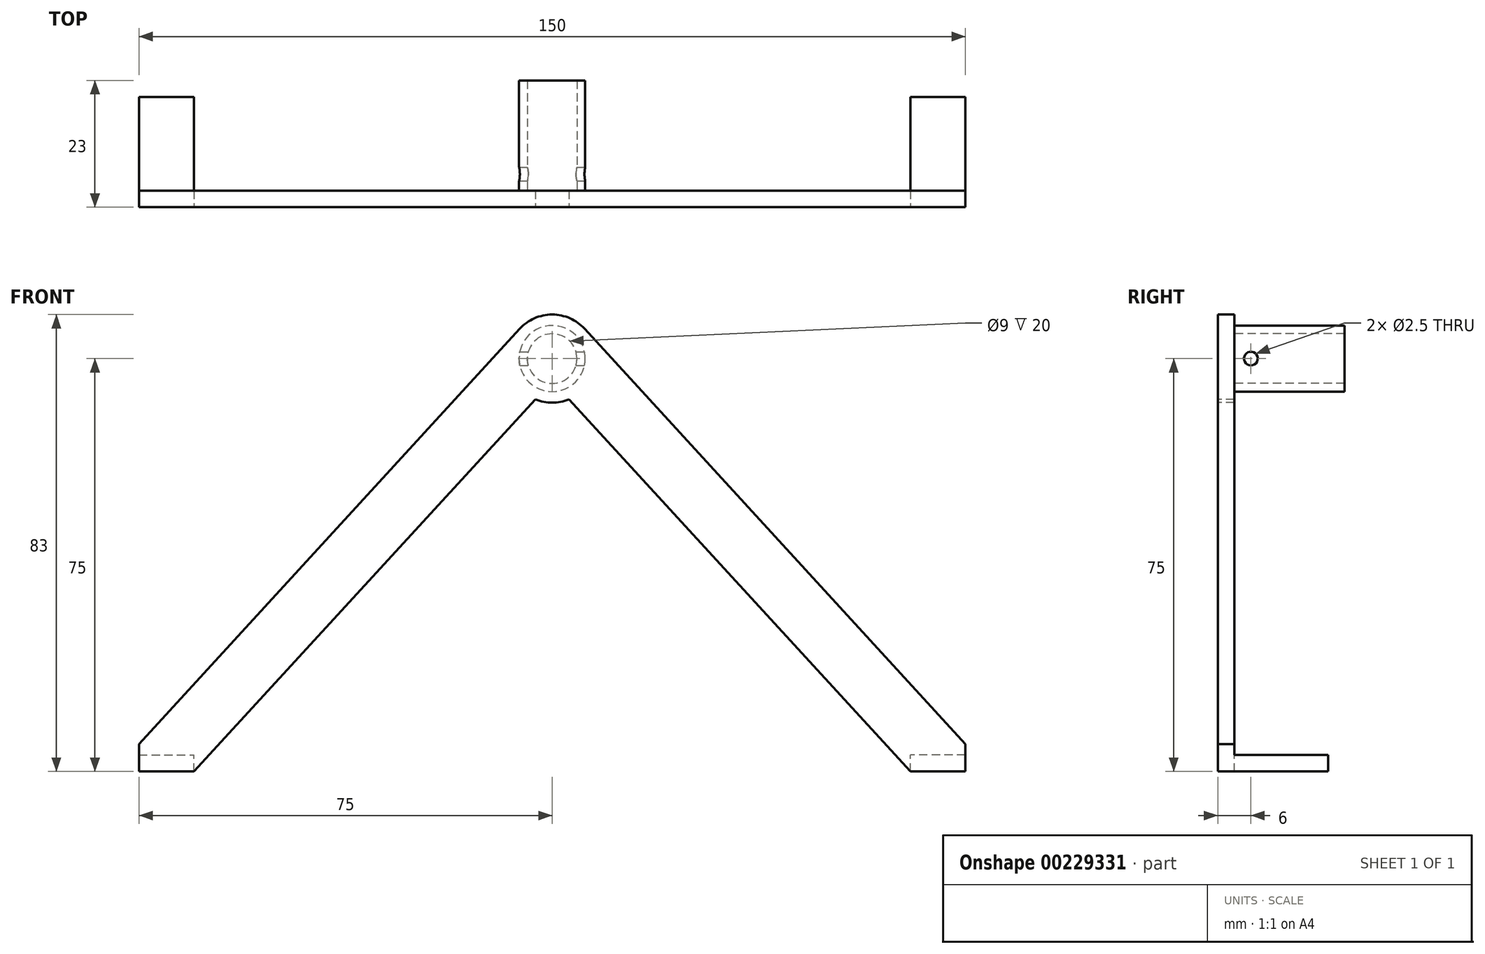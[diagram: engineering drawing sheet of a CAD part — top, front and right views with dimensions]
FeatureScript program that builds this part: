
annotation { "Feature Type Name" : "Feature", "Feature Type Description" : "" }
export const myFeature = defineFeature(function(context is Context, id is Id, definition is map)
    precondition{}
    {
        {
            var Q0;
            Q0=qCreatedBy(makeId("Front.planeOp"),FACE);
            var sketch = newSketch(context, id + "F0", { "sketchPlane" : qUnion([Q0])});
            skLineSegment(sketch, "E0", {"start": v(-75, 0) * mm, "end": v(-65, 0) * mm});
            skLineSegment(sketch, "E1", {"start": v(-75, 0) * mm, "end": v(-75, 5) * mm});
            skLineSegment(sketch, "E2", {"start": v(-75, 5) * mm, "end": v(-5.9, 80.4) * mm});
            skLineSegment(sketch, "E3.MirrorCS", {"start": v(75, 5) * mm, "end": v(5.9, 80.4) * mm});
            skLineSegment(sketch, "E4.MirrorCS", {"start": v(75, 0) * mm, "end": v(75, 5) * mm});
            skCircle(sketch, "E5", {"center": v(0, 75) * mm, "radius": 6 * mm, "construction": true});
            skArc(sketch, "E6", {"start": v(-3.05, 67.6) * mm, "mid": v(0, 67) * mm, "end": v(3.05, 67.6) * mm});
            skLineSegment(sketch, "E7", {"start": v(-65, 0) * mm, "end": v(-3.05, 67.6) * mm});
            skLineSegment(sketch, "E8.MirrorCS", {"start": v(65, 0) * mm, "end": v(3.05, 67.6) * mm});
            skArc(sketch, "E9.trimOffspring", {"start": v(5.9, 80.4) * mm, "mid": v(0, 83) * mm, "end": v(-5.9, 80.4) * mm});
            skLineSegment(sketch, "E10.trimOffspring", {"start": v(65, 0) * mm, "end": v(75, 0) * mm});
            skSolve(sketch);
        }
        {
            var Q0;
            Q0=makeQuery(id+"F0.imprint","IMPRINT",FACE,{"disambiguationData":[TD([[makeQuery(id+"F0.imprint","IMPRINT",EDGE,{"derivedFrom":sQuery(id+"F0.wireOp",EDGE,"E0")}),1.0]])]});
            extrude(context, id + "F1", {"entities" : qUnion([Q0]), "oppositeDirection" : true, "depth" : 3 * mm});
        }
        {
            var Q0;
            Q0=makeQuery(id+"F1.opExtrude","CAP_FACE",FACE,{"disambiguationData":[OSD([sQuery(id+"F0.wireOp",EDGE,"E0"),sQuery(id+"F0.wireOp",EDGE,"E1"),sQuery(id+"F0.wireOp",EDGE,"E2"),sQuery(id+"F0.wireOp",EDGE,"E3.MirrorCS"),sQuery(id+"F0.wireOp",EDGE,"E4.MirrorCS"),sQuery(id+"F0.wireOp",EDGE,"E6"),sQuery(id+"F0.wireOp",EDGE,"E7"),sQuery(id+"F0.wireOp",EDGE,"E8.MirrorCS"),sQuery(id+"F0.wireOp",EDGE,"E9.trimOffspring"),sQuery(id+"F0.wireOp",EDGE,"E10.trimOffspring")])],"isStart":false});
            var sketch = newSketch(context, id + "F2", { "sketchPlane" : qUnion([Q0])});
            skCircle(sketch, "E11", {"center": v(0, 75) * mm, "radius": 6 * mm});
            skCircle(sketch, "E12", {"center": v(0, 75) * mm, "radius": 4.5 * mm});
            skSolve(sketch);
        }
        {
            var Q0;
            Q0 = qSketchRegion(id + "F2", true);
            extrude(context, id + "F3", {"entities" : qUnion([Q0]), "operationType" : NewBodyOperationType.ADD, "depth" : 20 * mm});
        }
        {
            var Q0;
            {var subQ0=sQuery(id+"F0.wireOp",EDGE,"E10.trimOffspring");var subQ1=sQuery(id+"F0.wireOp",EDGE,"E8.MirrorCS");var subQ2=sQuery(id+"F0.wireOp",EDGE,"E7");var subQ3=sQuery(id+"F0.wireOp",EDGE,"E6");var subQ4=sQuery(id+"F0.wireOp",EDGE,"E4.MirrorCS");var subQ5=sQuery(id+"F0.wireOp",EDGE,"E0");var subQ6=sQuery(id+"F0.wireOp",EDGE,"E9.trimOffspring");var subQ7=sQuery(id+"F0.wireOp",EDGE,"E1");var subQ8=sQuery(id+"F0.wireOp",EDGE,"E2");var subQ9=sQuery(id+"F0.wireOp",EDGE,"E3.MirrorCS");Q0=makeQuery(id+"F3.boolean.opBoolean","SPLIT",FACE,{"disambiguationData":[TD([makeQuery(id+"F1.opExtrude","SWEPT_FACE",FACE,{"disambiguationData":[OSD([subQ5])]})])],"derivedFrom":makeQuery(id+"F1.opExtrude","CAP_FACE",FACE,{"disambiguationData":[OSD([subQ5,subQ7,subQ8,subQ9,subQ4,subQ3,subQ2,subQ1,subQ6,subQ0])],"isStart":false})});}
            var sketch = newSketch(context, id + "F4", { "sketchPlane" : qUnion([Q0])});
            skLineSegment(sketch, "E13.bottom", {"start": v(-75, 0) * mm, "end": v(-65, 0) * mm});
            skLineSegment(sketch, "E13.top", {"start": v(-75, 3) * mm, "end": v(-65, 3) * mm});
            skLineSegment(sketch, "E13.left", {"start": v(-75, 0) * mm, "end": v(-75, 3) * mm});
            skLineSegment(sketch, "E13.right", {"start": v(-65, 0) * mm, "end": v(-65, 3) * mm});
            skLineSegment(sketch, "E14.bottom", {"start": v(75, 0) * mm, "end": v(65, 0) * mm});
            skLineSegment(sketch, "E14.top", {"start": v(75, 3) * mm, "end": v(65, 3) * mm});
            skLineSegment(sketch, "E14.left", {"start": v(75, 0) * mm, "end": v(75, 3) * mm});
            skLineSegment(sketch, "E14.right", {"start": v(65, 0) * mm, "end": v(65, 3) * mm});
            skSolve(sketch);
        }
        {
            var Q0;
            Q0 = qSketchRegion(id + "F4", true);
            extrude(context, id + "F5", {"entities" : qUnion([Q0]), "operationType" : NewBodyOperationType.ADD, "depth" : 17 * mm});
        }
        {
            var Q0;
            Q0=qCreatedBy(makeId("Right.planeOp"),FACE);
            var sketch = newSketch(context, id + "F6", { "sketchPlane" : qUnion([Q0])});
            skCircle(sketch, "E15", {"center": v(6, 75) * mm, "radius": 1.25 * mm});
            skSolve(sketch);
        }
        {
            var Q0;
            Q0 = qSketchRegion(id + "F6", true);
            extrude(context, id + "F7", {"entities" : qUnion([Q0]), "operationType" : NewBodyOperationType.REMOVE, "oppositeDirection" : true, "depth" : 25 * mm, "symmetric" : true});
        }
    });
